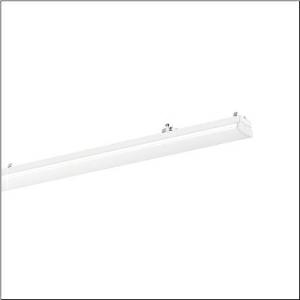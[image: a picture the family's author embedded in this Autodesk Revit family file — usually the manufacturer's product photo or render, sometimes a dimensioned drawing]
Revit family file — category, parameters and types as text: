
# Revit family: licross_r__11_recessed_opal_mo_51te1ddv4e5g_7031
name_source: partatom
category: Lighting Fixtures
units: mm (PartAtom-declared; Revit-internal decimal feet)

## family parameters
Cut with Voids When Loaded = No
Host = Face
Light Source = No
Part Type = Normal
Room Calculation Point = No
Round Connector Dimension = Use Diameter
Shared = No

## types (1)
- --- (1 x LED, 14560 lm, 84.1 W, 4000K)
    Apparent Load = 84 VA
    CIE Flux Codes = 44 73 91 87 100
    Color Rendering = 80
    Color Temperature = 4000K
    Default Elevation = 1800 mm
    Description = Licross® 11 recessed opal MO, luminaire insert, of sheet steel, coil coated, white, length: 2.250mm, width: 76mm, height: 87mm, LED rated luminous flux: 14.560lm, light colour: 840, control gear: DALI 2, with plug, 5-pole, with phase selection, mains connection: 220..240V, AC, 50/60Hz, rated input power: 84W, internal wiring halogen-free, primary optical cover: cover, of PMMA, light emission: direct with ceiling illumination distribution, primary light characteristic: symmetric, protection rating (complete): IP54, insulation class (complete): insulation class I (protective earthing), certification: CE, ENEC, VDE, UKCA, protection symbol: D if used in an environment with non-conductive dust loads with corresponding accessories, impact resistance: IK06, permissible ambient temperature for indoor applications: -25..+35°C, corresponds to IFS (International Featured Standards) requirements for safety and quality in the food industry, reducing of maximum allowable ambient temperature of 5°C with ceiling mounting, LABS conformity tested according to VDMA 24364:2018-05, packaging unit: 1 piece
    Height = 83 mm
    Lamp = 1 x LED
    Lamp Light Flux = 14560 lm
    Lamp Power = 84.1 W
    Lamp count = 1
    Length = 2250 mm
    Luminous efficacy = 173 lm/W
    Manufacturer = Siteco
    ModVariant = No
    Model = 51TE1DDV4E5G
    Mounting Place = Ceiling
    Mounting Type = Pendant
    Number of Poles = 1
    OnlyDefault = Yes
    Power Factor = 1
    Product Name = Licross® 11 recessed opal MO
    Product group = luminaire insert | ceiling pendant
    ProductGroupID = 902
    Protection Class = Protection class I
    Protection Degree = IP 54
    RLX_Detail_Level = 1
    RLX_Emergency_Light_Flux = 0 lm
    RLX_Emergency_Type = 0
    RLX_Emergency_Type_DB = No
    RlxData = <blob elided: 26837 chars, md5=2eb4fa4c>
    Socket = socket
    Standby Power = 0 W
    System Light Flux = 14560 lm
    System Power = 84 W
    Type Comments = factory setting: luminous flux: 100 % | dim-lin: 254 | 378 mA
    Type Image = l_1313666.jpg
    URL = http://relux.com
    VarID = @adj_097869
    Voltage = 0 V
    Weight = 0.00 kg
    Width = 76 mm

## geometry (parser evidence)
native form markers: Blend x4, Sweep x13
no freeform markers — native parametric forms only
